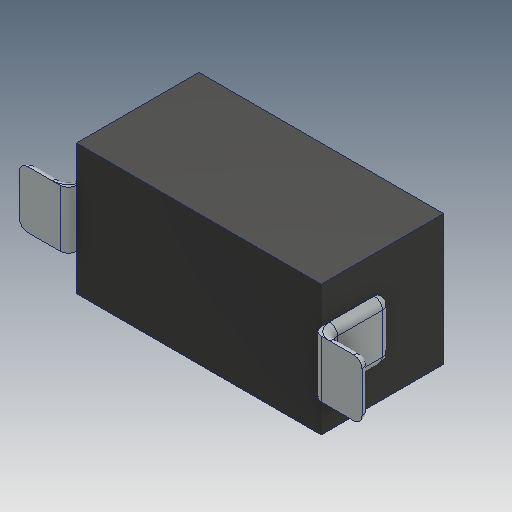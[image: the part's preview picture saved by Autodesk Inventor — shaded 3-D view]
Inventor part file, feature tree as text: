
AUTODESK INVENTOR PART (.ipt)
format: ipt  version: 2018 (Build 220112000, 112)  size: 133,120 bytes
history: native  units: mm
features: mirror x1
ambient origin geometry x8: Origin, YZ Plane, XZ Plane, XY Plane, X Axis, Y Axis, Z Axis, Center Point
bodies: Volumenkörper1 (feature_tree)
feature tree (1):
  mirror  "Mirror1"
